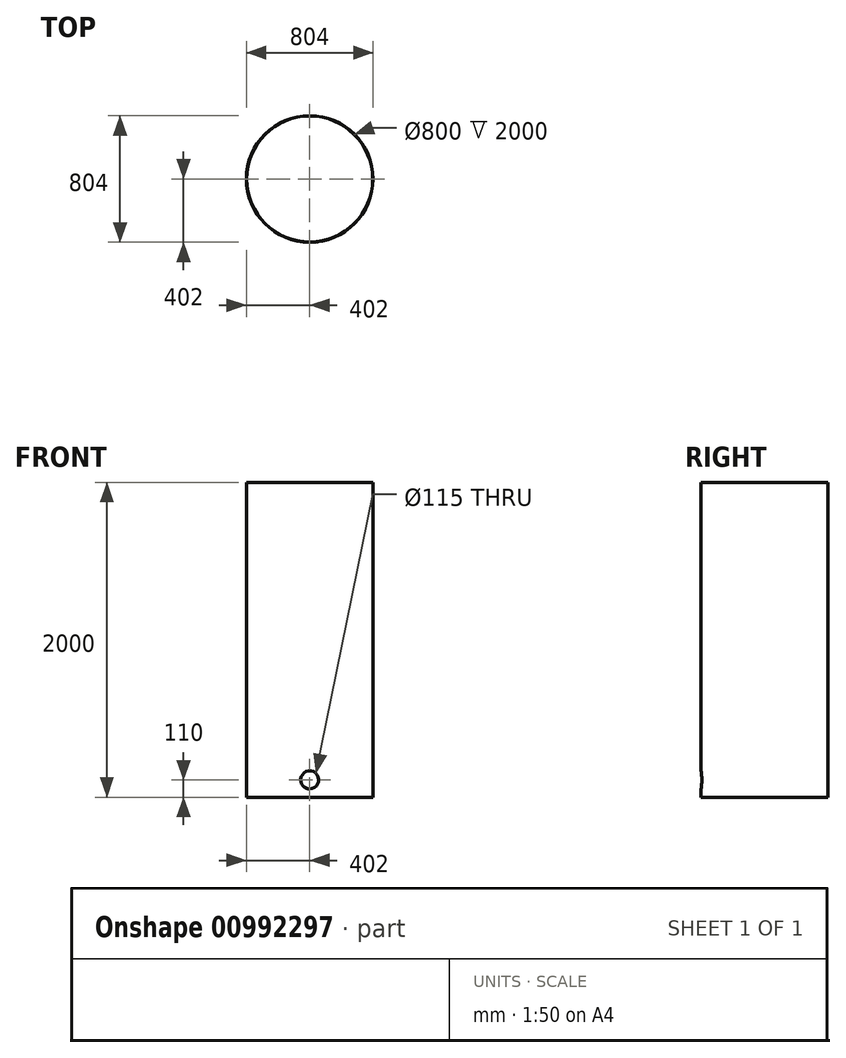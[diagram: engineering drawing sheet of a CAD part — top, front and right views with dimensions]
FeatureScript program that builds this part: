
annotation { "Feature Type Name" : "Feature", "Feature Type Description" : "" }
export const myFeature = defineFeature(function(context is Context, id is Id, definition is map)
    precondition{}
    {
        {
            var Q0;
            Q0=qCreatedBy(makeId("Top.planeOp"),FACE);
            var sketch = newSketch(context, id + "F0", { "sketchPlane" : qUnion([Q0])});
            skCircle(sketch, "E0", {"center": v(0, 0) * mm, "radius": 402 * mm});
            skCircle(sketch, "E1", {"center": v(0, 0) * mm, "radius": 400 * mm});
            skSolve(sketch);
        }
        {
            var Q0;
            Q0 = qSketchRegion(id + "F0", true);
            extrude(context, id + "F1", {"entities" : qUnion([Q0]), "depth" : 2000 * mm, "offsetDistance" : 25 * mm});
        }
        {
            var Q0;
            Q0=qCreatedBy(makeId("Front.planeOp"),FACE);
            var sketch = newSketch(context, id + "F2", { "sketchPlane" : qUnion([Q0])});
            skLineSegment(sketch, "E2", {"start": v(0, 0) * mm, "end": v(0, 110) * mm, "construction": true});
            skCircle(sketch, "E3", {"center": v(0, 110) * mm, "radius": 57.5 * mm});
            skSolve(sketch);
        }
        {
            var Q0;
            Q0 = qSketchRegion(id + "F2", true);
            extrude(context, id + "F3", {"entities" : qUnion([Q0]), "operationType" : NewBodyOperationType.ADD, "depth" : 500 * mm, "offsetDistance" : 25 * mm});
        }
        {
            var Q0;
            Q0=makeQuery(id+"F3.opExtrude","CAP_FACE",FACE,{"disambiguationData":[OSD([sQuery(id+"F2.wireOp",EDGE,"E3")])],"isStart":false});
            extrude(context, id + "F4", {"entities" : qUnion([Q0]), "operationType" : NewBodyOperationType.REMOVE, "endBound" : BoundingType.UP_TO_NEXT, "oppositeDirection" : true, "depth" : 25 * mm, "offsetDistance" : 25 * mm});
        }
    });
